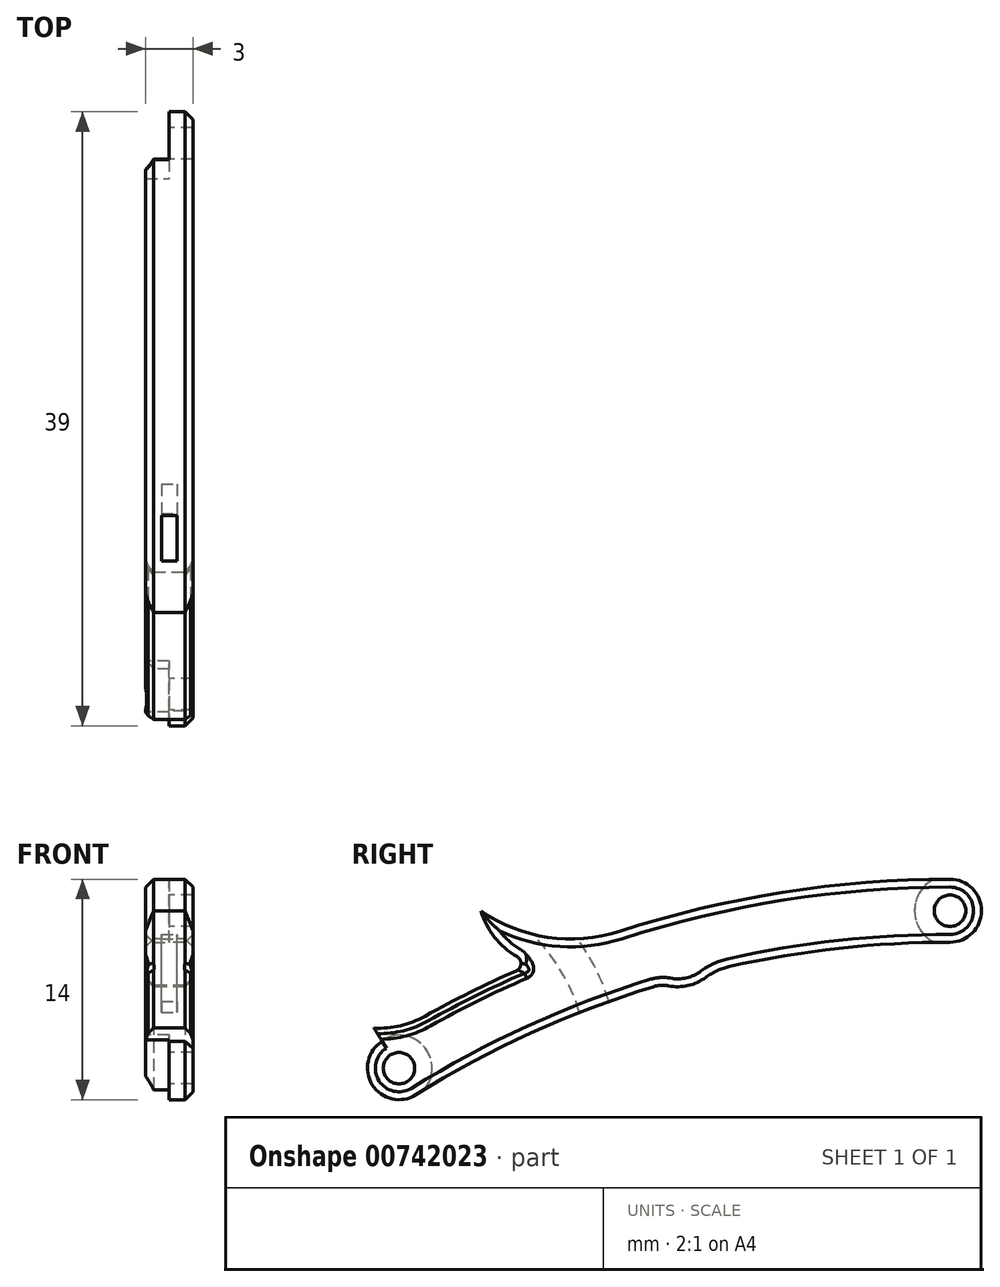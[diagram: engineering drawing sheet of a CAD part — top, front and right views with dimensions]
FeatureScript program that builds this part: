
annotation { "Feature Type Name" : "Feature", "Feature Type Description" : "" }
export const myFeature = defineFeature(function(context is Context, id is Id, definition is map)
    precondition{}
    {
        {
            var Q0;
            Q0=qCreatedBy(makeId("Right.planeOp"),FACE);
            var sketch = newSketch(context, id + "F0", { "sketchPlane" : qUnion([Q0])});
            skCircle(sketch, "E0", {"center": v(0, 0) * mm, "radius": 2 * mm});
            skArc(sketch, "E1", {"start": v(0, 2) * mm, "mid": v(-18.75, -0.63) * mm, "end": v(-36.06, -8.3) * mm});
            skArc(sketch, "E2", {"start": v(0, -2) * mm, "mid": v(-17.65, -4.47) * mm, "end": v(-33.94, -11.7) * mm});
            skCircle(sketch, "E3", {"center": v(-35, -10) * mm, "radius": 2 * mm});
            skArc(sketch, "E4", {"start": v(-29.8, 0) * mm, "mid": v(-25.55, -1.69) * mm, "end": v(-21, -1.31) * mm});
            skArc(sketch, "E5", {"start": v(-29.8, 0) * mm, "mid": v(-28.57, -2.09) * mm, "end": v(-26.5, -3.35) * mm});
            skLineSegment(sketch, "E6", {"start": v(-33.94, -11.7) * mm, "end": v(-36.58, -7.45) * mm});
            skArc(sketch, "E7", {"start": v(-36.58, -7.45) * mm, "mid": v(-34.9, -7.3) * mm, "end": v(-33.34, -6.7) * mm});
            skArc(sketch, "E8", {"start": v(-17.87, -4.77) * mm, "mid": v(-18.35, -4.74) * mm, "end": v(-18.83, -4.82) * mm});
            skArc(sketch, "E9", {"start": v(-17.87, -4.77) * mm, "mid": v(-16.63, -4.75) * mm, "end": v(-15.51, -4.23) * mm});
            skArc(sketch, "E10", {"start": v(-14, -3.54) * mm, "mid": v(-14.8, -3.81) * mm, "end": v(-15.51, -4.23) * mm});
            skSolve(sketch);
        }
        {
            var Q0;
            Q0 = qSketchRegion(id + "F0", true);
            extrude(context, id + "F1", {"entities" : qUnion([Q0]), "depth" : 3 * mm, "offsetDistance" : 25 * mm});
        }
        {
            var Q0;
            Q0=makeQuery(id+"F1.opExtrude","CAP_FACE",FACE,{"disambiguationData":[OSD([sQuery(id+"F0.wireOp",EDGE,"E0"),sQuery(id+"F0.wireOp",EDGE,"E1"),sQuery(id+"F0.wireOp",EDGE,"E2"),sQuery(id+"F0.wireOp",EDGE,"E3"),sQuery(id+"F0.wireOp",EDGE,"E4"),sQuery(id+"F0.wireOp",EDGE,"E5"),sQuery(id+"F0.wireOp",EDGE,"E6"),sQuery(id+"F0.wireOp",EDGE,"E7"),sQuery(id+"F0.wireOp",EDGE,"E8"),sQuery(id+"F0.wireOp",EDGE,"E9"),sQuery(id+"F0.wireOp",EDGE,"E10")])],"isStart":false});
            var sketch = newSketch(context, id + "F2", { "sketchPlane" : qUnion([Q0])});
            skCircle(sketch, "E11", {"center": v(0, 0) * mm, "radius": 2 * mm, "construction": true});
            skCircle(sketch, "E12", {"center": v(0, 0) * mm, "radius": 2.25 * mm});
            skSolve(sketch);
        }
        {
            var Q0;
            {var subQ2=sQuery(id+"F0.wireOp",EDGE,"E0");var subQ8=makeQuery(id+"F1.opExtrude","CAP_EDGE",EDGE,{"disambiguationData":[OSD([subQ2])],"isStart":false});Q0=makeQuery(id+"F2.imprint","IMPRINT",FACE,{"disambiguationData":[TD([[makeQuery(id+"F2.imprint","IMPRINT",EDGE,{"derivedFrom":subQ8}),1.0]])]});}
            var Q1;
            Q1=makeQuery(id+"F1.opExtrude","CAP_FACE",FACE,{"disambiguationData":[OSD([sQuery(id+"F0.wireOp",EDGE,"E0"),sQuery(id+"F0.wireOp",EDGE,"E1"),sQuery(id+"F0.wireOp",EDGE,"E2"),sQuery(id+"F0.wireOp",EDGE,"E3"),sQuery(id+"F0.wireOp",EDGE,"E4"),sQuery(id+"F0.wireOp",EDGE,"E5"),sQuery(id+"F0.wireOp",EDGE,"E6"),sQuery(id+"F0.wireOp",EDGE,"E7"),sQuery(id+"F0.wireOp",EDGE,"E8"),sQuery(id+"F0.wireOp",EDGE,"E9"),sQuery(id+"F0.wireOp",EDGE,"E10")])],"isStart":true});
            var Q2;
            Q2=sQuery(id+"F2.wireOp",EDGE,"E11");
            extrude(context, id + "F3", {"entities" : qUnion([Q0, Q1]), "operationType" : NewBodyOperationType.REMOVE, "surfaceEntities" : qUnion([Q2]), "oppositeDirection" : true, "depth" : 25 * mm, "offsetDistance" : 25 * mm, "hasSecondDirection" : true, "secondDirectionOppositeDirection" : true, "secondDirectionDepth" : 1.5 * mm});
        }
        {
            var Q0;
            Q0=makeQuery(id+"F3.boolean.opBoolean","COPY",FACE,{"derivedFrom":makeQuery(id+"F3.opExtrude","CAP_FACE",FACE,{"disambiguationData":[OSD([sQuery(id+"F0.wireOp",EDGE,"E0"),sQuery(id+"F0.wireOp",EDGE,"E1"),sQuery(id+"F0.wireOp",EDGE,"E2"),sQuery(id+"F2.wireOp",EDGE,"E12")])],"isStart":true})});
            var sketch = newSketch(context, id + "F4", { "sketchPlane" : qUnion([Q0])});
            skCircle(sketch, "E13", {"center": v(0, 0) * mm, "radius": 1 * mm});
            skSolve(sketch);
        }
        {
            var Q0;
            Q0 = qSketchRegion(id + "F4", true);
            extrude(context, id + "F5", {"entities" : qUnion([Q0]), "operationType" : NewBodyOperationType.REMOVE, "oppositeDirection" : true, "depth" : 25 * mm, "offsetDistance" : 25 * mm});
        }
        {
            var Q0;
            Q0=makeQuery(id+"F1.opExtrude","CAP_EDGE",EDGE,{"disambiguationData":[OSD([sQuery(id+"F0.wireOp",EDGE,"E4")])],"isStart":true});
            var Q1;
            {var subQ0=sQuery(id+"F0.wireOp",EDGE,"E2");Q1=makeQuery(id+"F1.opExtrude","CAP_EDGE",EDGE,{"disambiguationData":[OSD([subQ0]),TDD([makeQuery(id+"F0.imprint","IMPRINT",EDGE,{"disambiguationData":[TD([[makeQuery(id+"F0.imprint","INTERSECT",VERTEX,{"derivedFrom":[sQuery(id+"F0.wireOp",EDGE,"E0"),subQ0]}),-1.0]])],"derivedFrom":subQ0})])],"isStart":true});}
            var Q2;
            Q2=makeQuery(id+"F1.opExtrude","CAP_EDGE",EDGE,{"disambiguationData":[OSD([sQuery(id+"F0.wireOp",EDGE,"E4")])],"isStart":false});
            chamfer(context, id + "F6", {"entities" : qUnion([Q0, Q1, Q2]), "width" : 0.5 * mm, "tangentPropagation" : true});
        }
        {
            var Q0;
            {var subQ0=sQuery(id+"F0.wireOp",EDGE,"E1");Q0=makeQuery(id+"F1.opExtrude","CAP_EDGE",EDGE,{"disambiguationData":[OSD([subQ0]),TDD([makeQuery(id+"F0.imprint","IMPRINT",EDGE,{"disambiguationData":[TD([[makeQuery(id+"F0.imprint","INTERSECT",VERTEX,{"derivedFrom":[subQ0,sQuery(id+"F0.wireOp",EDGE,"E5")]}),-1.0]])],"derivedFrom":subQ0})])],"isStart":true});}
            var Q1;
            {var subQ0=sQuery(id+"F0.wireOp",EDGE,"E1");Q1=makeQuery(id+"F1.opExtrude","CAP_EDGE",EDGE,{"disambiguationData":[OSD([subQ0]),TDD([makeQuery(id+"F0.imprint","IMPRINT",EDGE,{"disambiguationData":[TD([[makeQuery(id+"F0.imprint","INTERSECT",VERTEX,{"derivedFrom":[subQ0,sQuery(id+"F0.wireOp",EDGE,"E5")]}),-1.0]])],"derivedFrom":subQ0})])],"isStart":false});}
            chamfer(context, id + "F7", {"entities" : qUnion([Q0, Q1]), "width" : 0.5 * mm, "tangentPropagation" : true});
        }
        {
            var Q0;
            Q0=makeQuery(id+"F1.opExtrude","SWEPT_EDGE",EDGE,{"disambiguationData":[OSD([sQuery(id+"F0.wireOp",EDGE,"E1"),sQuery(id+"F0.wireOp",EDGE,"E5")])]});
            var Q1;
            {var subQ0=sQuery(id+"F0.wireOp",EDGE,"E5");var subQ1=sQuery(id+"F0.wireOp",EDGE,"E1");Q1=makeQuery(id+"F7.opChamfer","BLEND_EDGE",EDGE,{"blendedFrom":[makeQuery(id+"F1.opExtrude","CAP_EDGE",EDGE,{"disambiguationData":[OSD([subQ1]),TDD([makeQuery(id+"F0.imprint","IMPRINT",EDGE,{"disambiguationData":[TD([[makeQuery(id+"F0.imprint","INTERSECT",VERTEX,{"derivedFrom":[subQ1,subQ0]}),-1.0]])],"derivedFrom":subQ1})])],"isStart":true}),makeQuery(id+"F1.opExtrude","SWEPT_FACE",FACE,{"disambiguationData":[OSD([subQ0])]})],"blendedInto":[makeQuery(id+"F1.opExtrude","SWEPT_FACE",FACE,{"disambiguationData":[OSD([subQ0])]})]});}
            var Q2;
            {var subQ0=sQuery(id+"F0.wireOp",EDGE,"E5");var subQ1=sQuery(id+"F0.wireOp",EDGE,"E1");Q2=makeQuery(id+"F7.opChamfer","BLEND_EDGE",EDGE,{"blendedFrom":[makeQuery(id+"F1.opExtrude","CAP_EDGE",EDGE,{"disambiguationData":[OSD([subQ1]),TDD([makeQuery(id+"F0.imprint","IMPRINT",EDGE,{"disambiguationData":[TD([[makeQuery(id+"F0.imprint","INTERSECT",VERTEX,{"derivedFrom":[subQ1,subQ0]}),-1.0]])],"derivedFrom":subQ1})])],"isStart":false}),makeQuery(id+"F1.opExtrude","SWEPT_FACE",FACE,{"disambiguationData":[OSD([subQ0])]})],"blendedInto":[makeQuery(id+"F1.opExtrude","SWEPT_FACE",FACE,{"disambiguationData":[OSD([subQ0])]})]});}
            fillet(context, id + "F8", {"entities" : qUnion([Q0, Q1, Q2]), "radius" : 0.5 * mm, "tangentPropagation" : true, "allowEdgeOverflow" : false});
        }
        {
            var Q0;
            {var subQ0=sQuery(id+"F0.wireOp",EDGE,"E7");var subQ1=sQuery(id+"F0.wireOp",EDGE,"E5");var subQ2=sQuery(id+"F0.wireOp",EDGE,"E1");Q0=makeQuery(id+"F8.opFillet","BLEND_EDGE",EDGE,{"blendedFrom":[makeQuery(id+"F7.opChamfer","BLEND_EDGE",EDGE,{"blendedFrom":[makeQuery(id+"F1.opExtrude","CAP_EDGE",EDGE,{"disambiguationData":[OSD([subQ2]),TDD([makeQuery(id+"F0.imprint","IMPRINT",EDGE,{"disambiguationData":[TD([[makeQuery(id+"F0.imprint","INTERSECT",VERTEX,{"derivedFrom":[subQ2,subQ1]}),-1.0]])],"derivedFrom":subQ2})])],"isStart":true}),makeQuery(id+"F1.opExtrude","SWEPT_FACE",FACE,{"disambiguationData":[OSD([subQ1])]})],"blendedInto":[makeQuery(id+"F1.opExtrude","SWEPT_FACE",FACE,{"disambiguationData":[OSD([subQ1])]})]}),makeQuery(id+"F1.opExtrude","CAP_FACE",FACE,{"disambiguationData":[OSD([sQuery(id+"F0.wireOp",EDGE,"E0"),subQ2,sQuery(id+"F0.wireOp",EDGE,"E2"),sQuery(id+"F0.wireOp",EDGE,"E3"),sQuery(id+"F0.wireOp",EDGE,"E4"),subQ1,sQuery(id+"F0.wireOp",EDGE,"E6"),subQ0,sQuery(id+"F0.wireOp",EDGE,"E8"),sQuery(id+"F0.wireOp",EDGE,"E9"),sQuery(id+"F0.wireOp",EDGE,"E10")])],"isStart":true})],"blendedInto":[makeQuery(id+"F1.opExtrude","CAP_FACE",FACE,{"disambiguationData":[OSD([sQuery(id+"F0.wireOp",EDGE,"E0"),subQ2,sQuery(id+"F0.wireOp",EDGE,"E2"),sQuery(id+"F0.wireOp",EDGE,"E3"),sQuery(id+"F0.wireOp",EDGE,"E4"),subQ1,sQuery(id+"F0.wireOp",EDGE,"E6"),subQ0,sQuery(id+"F0.wireOp",EDGE,"E8"),sQuery(id+"F0.wireOp",EDGE,"E9"),sQuery(id+"F0.wireOp",EDGE,"E10")])],"isStart":true})]});}
            var Q1;
            Q1=makeQuery(id+"F1.opExtrude","CAP_EDGE",EDGE,{"disambiguationData":[OSD([sQuery(id+"F0.wireOp",EDGE,"E5")])],"isStart":true});
            var Q2;
            {var subQ0=sQuery(id+"F0.wireOp",EDGE,"E7");var subQ1=sQuery(id+"F0.wireOp",EDGE,"E5");var subQ2=sQuery(id+"F0.wireOp",EDGE,"E1");Q2=makeQuery(id+"F8.opFillet","BLEND_EDGE",EDGE,{"blendedFrom":[makeQuery(id+"F7.opChamfer","BLEND_EDGE",EDGE,{"blendedFrom":[makeQuery(id+"F1.opExtrude","CAP_EDGE",EDGE,{"disambiguationData":[OSD([subQ2]),TDD([makeQuery(id+"F0.imprint","IMPRINT",EDGE,{"disambiguationData":[TD([[makeQuery(id+"F0.imprint","INTERSECT",VERTEX,{"derivedFrom":[subQ2,subQ1]}),-1.0]])],"derivedFrom":subQ2})])],"isStart":false}),makeQuery(id+"F1.opExtrude","SWEPT_FACE",FACE,{"disambiguationData":[OSD([subQ1])]})],"blendedInto":[makeQuery(id+"F1.opExtrude","SWEPT_FACE",FACE,{"disambiguationData":[OSD([subQ1])]})]}),makeQuery(id+"F1.opExtrude","CAP_FACE",FACE,{"disambiguationData":[OSD([sQuery(id+"F0.wireOp",EDGE,"E0"),subQ2,sQuery(id+"F0.wireOp",EDGE,"E2"),sQuery(id+"F0.wireOp",EDGE,"E3"),sQuery(id+"F0.wireOp",EDGE,"E4"),subQ1,sQuery(id+"F0.wireOp",EDGE,"E6"),subQ0,sQuery(id+"F0.wireOp",EDGE,"E8"),sQuery(id+"F0.wireOp",EDGE,"E9"),sQuery(id+"F0.wireOp",EDGE,"E10")])],"isStart":false})],"blendedInto":[makeQuery(id+"F1.opExtrude","CAP_FACE",FACE,{"disambiguationData":[OSD([sQuery(id+"F0.wireOp",EDGE,"E0"),subQ2,sQuery(id+"F0.wireOp",EDGE,"E2"),sQuery(id+"F0.wireOp",EDGE,"E3"),sQuery(id+"F0.wireOp",EDGE,"E4"),subQ1,sQuery(id+"F0.wireOp",EDGE,"E6"),subQ0,sQuery(id+"F0.wireOp",EDGE,"E8"),sQuery(id+"F0.wireOp",EDGE,"E9"),sQuery(id+"F0.wireOp",EDGE,"E10")])],"isStart":false})]});}
            var Q3;
            Q3=makeQuery(id+"F1.opExtrude","CAP_EDGE",EDGE,{"disambiguationData":[OSD([sQuery(id+"F0.wireOp",EDGE,"E5")])],"isStart":false});
            chamfer(context, id + "F9", {"entities" : qUnion([Q0, Q1, Q2, Q3]), "width" : 0.5 * mm, "tangentPropagation" : true});
        }
        {
            var Q0;
            Q0=makeQuery(id+"F1.opExtrude","CAP_FACE",FACE,{"disambiguationData":[OSD([sQuery(id+"F0.wireOp",EDGE,"E0"),sQuery(id+"F0.wireOp",EDGE,"E1"),sQuery(id+"F0.wireOp",EDGE,"E2"),sQuery(id+"F0.wireOp",EDGE,"E3"),sQuery(id+"F0.wireOp",EDGE,"E4"),sQuery(id+"F0.wireOp",EDGE,"E5"),sQuery(id+"F0.wireOp",EDGE,"E6"),sQuery(id+"F0.wireOp",EDGE,"E7"),sQuery(id+"F0.wireOp",EDGE,"E8"),sQuery(id+"F0.wireOp",EDGE,"E9"),sQuery(id+"F0.wireOp",EDGE,"E10")])],"isStart":true});
            var sketch = newSketch(context, id + "F10", { "sketchPlane" : qUnion([Q0])});
            skCircle(sketch, "E14", {"center": v(35, -10) * mm, "radius": 2.1 * mm});
            skCircle(sketch, "E15", {"center": v(35, -10) * mm, "radius": 2 * mm, "construction": true});
            skSolve(sketch);
        }
        {
            var Q0;
            Q0 = qSketchRegion(id + "F10", true);
            extrude(context, id + "F11", {"entities" : qUnion([Q0]), "operationType" : NewBodyOperationType.REMOVE, "oppositeDirection" : true, "depth" : 1.5 * mm, "offsetDistance" : 25 * mm});
        }
        {
            var Q0;
            Q0=makeQuery(id+"F11.boolean.opBoolean","COPY",FACE,{"derivedFrom":makeQuery(id+"F11.opExtrude","CAP_FACE",FACE,{"disambiguationData":[OSD([sQuery(id+"F10.wireOp",EDGE,"E14")])],"isStart":false})});
            var sketch = newSketch(context, id + "F12", { "sketchPlane" : qUnion([Q0])});
            skCircle(sketch, "E16", {"center": v(35, -10) * mm, "radius": 1 * mm});
            skSolve(sketch);
        }
        {
            var Q0;
            Q0 = qSketchRegion(id + "F12", true);
            extrude(context, id + "F13", {"entities" : qUnion([Q0]), "operationType" : NewBodyOperationType.REMOVE, "oppositeDirection" : true, "depth" : 25 * mm, "offsetDistance" : 25 * mm});
        }
        {
            var Q0;
            Q0=makeQuery(id+"F1.opExtrude","CAP_FACE",FACE,{"disambiguationData":[OSD([sQuery(id+"F0.wireOp",EDGE,"E0"),sQuery(id+"F0.wireOp",EDGE,"E1"),sQuery(id+"F0.wireOp",EDGE,"E2"),sQuery(id+"F0.wireOp",EDGE,"E3"),sQuery(id+"F0.wireOp",EDGE,"E4"),sQuery(id+"F0.wireOp",EDGE,"E5"),sQuery(id+"F0.wireOp",EDGE,"E6"),sQuery(id+"F0.wireOp",EDGE,"E7"),sQuery(id+"F0.wireOp",EDGE,"E8"),sQuery(id+"F0.wireOp",EDGE,"E9"),sQuery(id+"F0.wireOp",EDGE,"E10")])],"isStart":false});
            var sketch = newSketch(context, id + "F14", { "sketchPlane" : qUnion([Q0])});
            skCircle(sketch, "E17", {"center": v(-35, -10) * mm, "radius": 13 * mm, "construction": true});
            skCircle(sketch, "E18", {"center": v(-35, -10) * mm, "radius": 14 * mm});
            skCircle(sketch, "E19", {"center": v(-35, -10) * mm, "radius": 12 * mm});
            skLineSegment(sketch, "E20", {"start": v(-23, -10) * mm, "end": v(-21, -10) * mm});
            skPoint(sketch, "E21", {"position": v(-22, -10) * mm});
            skSolve(sketch);
        }
        {
            var Q0;
            Q0 = qSketchRegion(id + "F14", true);
            extrude(context, id + "F15", {"entities" : qUnion([Q0]), "operationType" : NewBodyOperationType.REMOVE, "oppositeDirection" : true, "depth" : 2 * mm, "offsetDistance" : 25 * mm, "hasSecondDirection" : true, "secondDirectionOppositeDirection" : true, "secondDirectionDepth" : 1 * mm});
        }
    });
